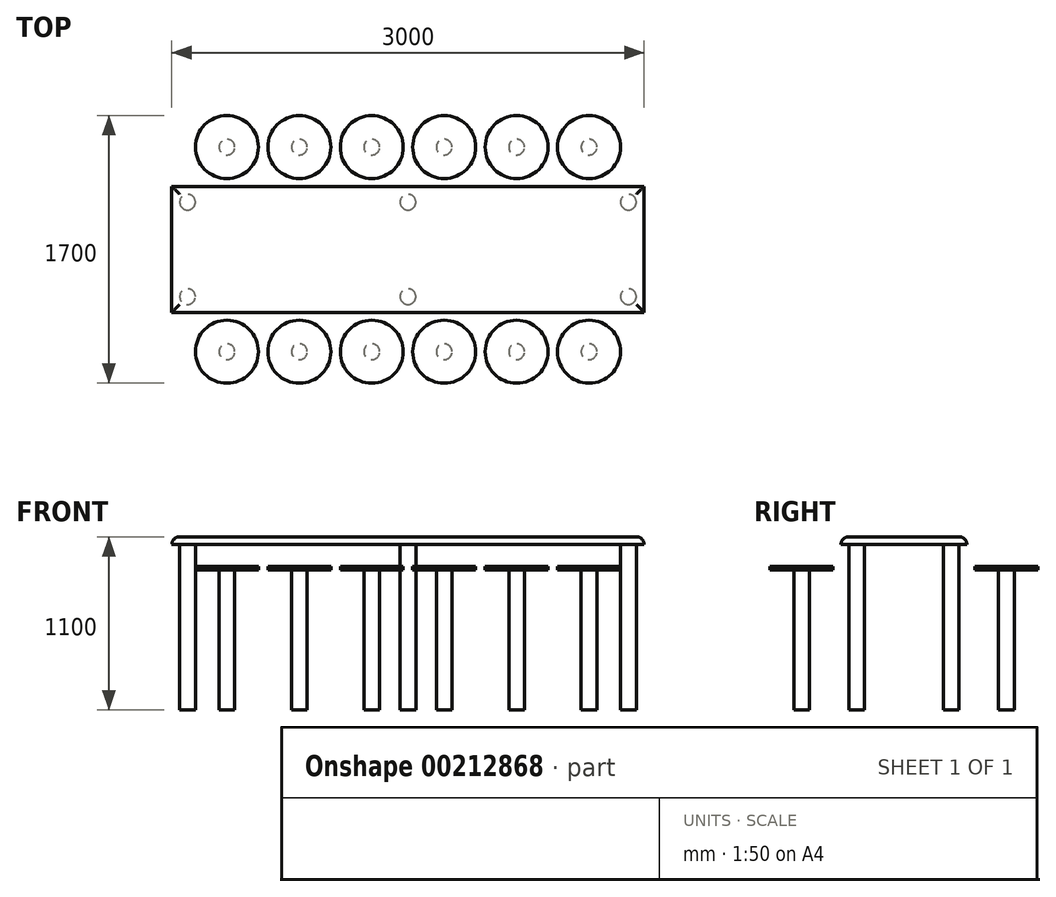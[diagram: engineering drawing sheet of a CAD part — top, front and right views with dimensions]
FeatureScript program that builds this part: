
annotation { "Feature Type Name" : "Feature", "Feature Type Description" : "" }
export const myFeature = defineFeature(function(context is Context, id is Id, definition is map)
    precondition{}
    {
        {
            var Q0;
            Q0=qCreatedBy(makeId("Front.planeOp"),FACE);
            var sketch = newSketch(context, id + "F0", { "sketchPlane" : qUnion([Q0])});
            skLineSegment(sketch, "E0.bottom", {"start": v(0, 50) * mm, "end": v(3000, 50) * mm});
            skLineSegment(sketch, "E0.top", {"start": v(0, 0) * mm, "end": v(3000, 0) * mm});
            skLineSegment(sketch, "E0.left", {"start": v(0, 50) * mm, "end": v(0, 0) * mm});
            skLineSegment(sketch, "E0.right", {"start": v(3000, 50) * mm, "end": v(3000, 0) * mm});
            skLineSegment(sketch, "E1.bottom", {"start": v(3000, 0) * mm, "end": v(2950, 0) * mm});
            skLineSegment(sketch, "E1.top", {"start": v(3000, -1050) * mm, "end": v(2950, -1050) * mm});
            skLineSegment(sketch, "E1.left", {"start": v(3000, 0) * mm, "end": v(3000, -1050) * mm});
            skLineSegment(sketch, "E1.right", {"start": v(2950, 0) * mm, "end": v(2950, -1050) * mm});
            skLineSegment(sketch, "E2.bottom", {"start": v(1500, 0) * mm, "end": v(1450, 0) * mm});
            skLineSegment(sketch, "E2.top", {"start": v(1500, -1050) * mm, "end": v(1450, -1050) * mm});
            skLineSegment(sketch, "E2.left", {"start": v(1500, 0) * mm, "end": v(1500, -1050) * mm});
            skLineSegment(sketch, "E2.right", {"start": v(1450, 0) * mm, "end": v(1450, -1050) * mm});
            skLineSegment(sketch, "E3.MirrorCS", {"start": v(0, -1050) * mm, "end": v(50, -1050) * mm});
            skLineSegment(sketch, "E4.MirrorCS", {"start": v(0, 0) * mm, "end": v(50, 0) * mm});
            skLineSegment(sketch, "E5.MirrorCS", {"start": v(0, 0) * mm, "end": v(0, -1050) * mm});
            skLineSegment(sketch, "E6.MirrorCS", {"start": v(50, 0) * mm, "end": v(50, -1050) * mm});
            skSolve(sketch);
        }
        {
            var Q0;
            Q0 = qSketchRegion(id + "F0", true);
            extrude(context, id + "F1", {"entities" : qUnion([Q0]), "depth" : 800 * mm});
        }
        {
            var Q0;
            Q0=makeQuery(id+"F1.opExtrude","SWEPT_EDGE",EDGE,{"disambiguationData":[OSD([sQuery(id+"F0.wireOp",EDGE,"E0.bottom"),sQuery(id+"F0.wireOp",EDGE,"E0.left")])]});
            var Q1;
            Q1=makeQuery(id+"F1.opExtrude","CAP_EDGE",EDGE,{"disambiguationData":[OSD([sQuery(id+"F0.wireOp",EDGE,"E0.bottom")])],"isStart":false});
            var Q2;
            Q2=makeQuery(id+"F1.opExtrude","CAP_EDGE",EDGE,{"disambiguationData":[OSD([sQuery(id+"F0.wireOp",EDGE,"E0.bottom")])],"isStart":true});
            var Q3;
            Q3=makeQuery(id+"F1.opExtrude","SWEPT_EDGE",EDGE,{"disambiguationData":[OSD([sQuery(id+"F0.wireOp",EDGE,"E0.bottom"),sQuery(id+"F0.wireOp",EDGE,"E0.right")])]});
            fillet(context, id + "F2", {"entities" : qUnion([Q0, Q1, Q2, Q3]), "radius" : 50 * mm, "tangentPropagation" : true, "allowEdgeOverflow" : false});
        }
        {
            var Q0;
            Q0=makeQuery(id+"F1.opExtrude","SWEPT_FACE",FACE,{"disambiguationData":[OSD([sQuery(id+"F0.wireOp",EDGE,"E3.MirrorCS")])]});
            var sketch = newSketch(context, id + "F3", { "sketchPlane" : qUnion([Q0])});
            skCircle(sketch, "E7", {"center": v(350, -250) * mm, "radius": 50 * mm});
            skCircle(sketch, "E8.0.1.0", {"center": v(350, 1050) * mm, "radius": 50 * mm});
            skCircle(sketch, "E8.1.0.0", {"center": v(810, -250) * mm, "radius": 50 * mm});
            skCircle(sketch, "E8.1.1.0", {"center": v(810, 1050) * mm, "radius": 50 * mm});
            skCircle(sketch, "E8.2.0.0", {"center": v(1270, -250) * mm, "radius": 50 * mm});
            skCircle(sketch, "E8.2.1.0", {"center": v(1270, 1050) * mm, "radius": 50 * mm});
            skCircle(sketch, "E8.3.0.0", {"center": v(1730, -250) * mm, "radius": 50 * mm});
            skCircle(sketch, "E8.3.1.0", {"center": v(1730, 1050) * mm, "radius": 50 * mm});
            skCircle(sketch, "E8.4.0.0", {"center": v(2190, -250) * mm, "radius": 50 * mm});
            skCircle(sketch, "E8.4.1.0", {"center": v(2190, 1050) * mm, "radius": 50 * mm});
            skCircle(sketch, "E8.5.0.0", {"center": v(2650, -250) * mm, "radius": 50 * mm});
            skCircle(sketch, "E8.5.1.0", {"center": v(2650, 1050) * mm, "radius": 50 * mm});
            skLineSegment(sketch, "E8.direction1", {"start": v(350, -250) * mm, "end": v(810, -250) * mm, "construction": true});
            skLineSegment(sketch, "E8.direction2", {"start": v(350, -250) * mm, "end": v(350, 1050) * mm, "construction": true});
            skSolve(sketch);
        }
        {
            var Q0;
            Q0 = qSketchRegion(id + "F3", true);
            extrude(context, id + "F4", {"entities" : qUnion([Q0]), "oppositeDirection" : true, "depth" : 900 * mm});
        }
        {
            var Q0;
            Q0=makeQuery(id+"F4.opExtrude","CAP_FACE",FACE,{"disambiguationData":[OSD([sQuery(id+"F3.wireOp",EDGE,"E7")])],"isStart":false});
            var sketch = newSketch(context, id + "F5", { "sketchPlane" : qUnion([Q0])});
            skCircle(sketch, "E9", {"center": v(350, 250) * mm, "radius": 200 * mm});
            skCircle(sketch, "E10.0.1.0", {"center": v(350, -1050) * mm, "radius": 200 * mm});
            skCircle(sketch, "E10.1.0.0", {"center": v(810, 250) * mm, "radius": 200 * mm});
            skCircle(sketch, "E10.1.1.0", {"center": v(810, -1050) * mm, "radius": 200 * mm});
            skCircle(sketch, "E10.2.0.0", {"center": v(1270, 250) * mm, "radius": 200 * mm});
            skCircle(sketch, "E10.2.1.0", {"center": v(1270, -1050) * mm, "radius": 200 * mm});
            skCircle(sketch, "E10.3.0.0", {"center": v(1730, 250) * mm, "radius": 200 * mm});
            skCircle(sketch, "E10.3.1.0", {"center": v(1730, -1050) * mm, "radius": 200 * mm});
            skCircle(sketch, "E10.4.0.0", {"center": v(2190, 250) * mm, "radius": 200 * mm});
            skCircle(sketch, "E10.4.1.0", {"center": v(2190, -1050) * mm, "radius": 200 * mm});
            skCircle(sketch, "E10.5.0.0", {"center": v(2650, 250) * mm, "radius": 200 * mm});
            skCircle(sketch, "E10.5.1.0", {"center": v(2650, -1050) * mm, "radius": 200 * mm});
            skLineSegment(sketch, "E10.direction1", {"start": v(350, 250) * mm, "end": v(810, 250) * mm, "construction": true});
            skLineSegment(sketch, "E10.direction2", {"start": v(350, 250) * mm, "end": v(350, -1050) * mm, "construction": true});
            skSolve(sketch);
        }
        {
            var Q0;
            Q0 = qSketchRegion(id + "F5", true);
            extrude(context, id + "F6", {"entities" : qUnion([Q0]), "endBound" : BoundingType.SYMMETRIC, "oppositeDirection" : true, "depth" : 25 * mm});
        }
        {
            var Q0;
            Q0=makeQuery(id+"F1.opExtrude","SWEPT_FACE",FACE,{"disambiguationData":[OSD([sQuery(id+"F0.wireOp",EDGE,"E0.left"),sQuery(id+"F0.wireOp",EDGE,"E5.MirrorCS")])]});
            var sketch = newSketch(context, id + "F7", { "sketchPlane" : qUnion([Q0])});
            skLineSegment(sketch, "E11.bottom", {"start": v(0, -1050) * mm, "end": v(800, -1050) * mm});
            skLineSegment(sketch, "E11.top", {"start": v(0, 0) * mm, "end": v(800, 0) * mm});
            skLineSegment(sketch, "E11.left", {"start": v(0, -1050) * mm, "end": v(0, 0) * mm});
            skLineSegment(sketch, "E11.right", {"start": v(800, -1050) * mm, "end": v(800, 0) * mm});
            skSolve(sketch);
        }
        {
            var Q0;
            Q0 = qSketchRegion(id + "F7", true);
            extrude(context, id + "F8", {"entities" : qUnion([Q0]), "operationType" : NewBodyOperationType.REMOVE, "endBound" : BoundingType.THROUGH_ALL, "oppositeDirection" : true, "depth" : 25 * mm});
        }
        {
            var Q0;
            {var subQ0=sQuery(id+"F0.wireOp",EDGE,"E0.top");Q0=makeQuery(id+"F8.boolean.opBoolean","MERGE",FACE,{"derivedFrom":[makeQuery(id+"F1.opExtrude","SWEPT_FACE",FACE,{"disambiguationData":[OSD([subQ0]),TDD([makeQuery(id+"F0.imprint","IMPRINT",EDGE,{"disambiguationData":[TD([[makeQuery(id+"F0.imprint","INTERSECT",VERTEX,{"derivedFrom":[subQ0,sQuery(id+"F0.wireOp",EDGE,"E4.MirrorCS"),sQuery(id+"F0.wireOp",EDGE,"E6.MirrorCS")]}),-1.0]])],"derivedFrom":subQ0})])]}),makeQuery(id+"F1.opExtrude","SWEPT_FACE",FACE,{"disambiguationData":[OSD([subQ0]),TDD([makeQuery(id+"F0.imprint","IMPRINT",EDGE,{"disambiguationData":[TD([[makeQuery(id+"F0.imprint","INTERSECT",VERTEX,{"derivedFrom":[subQ0,sQuery(id+"F0.wireOp",EDGE,"E1.bottom"),sQuery(id+"F0.wireOp",EDGE,"E1.right")]}),1.0]])],"derivedFrom":subQ0})])]}),makeQuery(id+"F8.opExtrude","SWEPT_FACE",FACE,{"disambiguationData":[OSD([sQuery(id+"F7.wireOp",EDGE,"E11.top")])]})]});}
            var sketch = newSketch(context, id + "F9", { "sketchPlane" : qUnion([Q0])});
            skCircle(sketch, "E12", {"center": v(100, 700) * mm, "radius": 50 * mm});
            skCircle(sketch, "E13.0.1.0", {"center": v(100, 100) * mm, "radius": 50 * mm});
            skCircle(sketch, "E13.1.0.0", {"center": v(1500, 700) * mm, "radius": 50 * mm});
            skCircle(sketch, "E13.1.1.0", {"center": v(1500, 100) * mm, "radius": 50 * mm});
            skCircle(sketch, "E13.2.0.0", {"center": v(2900, 700) * mm, "radius": 50 * mm});
            skCircle(sketch, "E13.2.1.0", {"center": v(2900, 100) * mm, "radius": 50 * mm});
            skLineSegment(sketch, "E13.direction1", {"start": v(100, 700) * mm, "end": v(1500, 700) * mm, "construction": true});
            skLineSegment(sketch, "E13.direction2", {"start": v(100, 700) * mm, "end": v(100, 100) * mm, "construction": true});
            skSolve(sketch);
        }
        {
            var Q0;
            Q0 = qSketchRegion(id + "F9", true);
            var Q1;
            Q1=makeQuery(id+"F4.opExtrude","CAP_FACE",FACE,{"disambiguationData":[OSD([sQuery(id+"F3.wireOp",EDGE,"E8.0.1.0")])],"isStart":true});
            extrude(context, id + "F10", {"entities" : qUnion([Q0]), "operationType" : NewBodyOperationType.ADD, "endBound" : BoundingType.UP_TO_SURFACE, "endBoundEntityFace" : qUnion([Q1]), "depth" : 25 * mm});
        }
    });
